# Revit family: DAL_A3-Gate-double
name_source: partatom
category: Doors
revit_build: Autodesk Revit 2016 (Build: 20150220_1215(x64)
units: mm (PartAtom-declared; Revit-internal decimal feet)

## family parameters
Always vertical = Yes
Cut with Voids When Loaded = No
Host = Wall
Room Calculation Point = No
Shared = No

## types (3) — shared parameters
Frame Projection Ext. = 25 mm  [stored 0.082021 ft]
Frame Projection Int. = 25 mm  [stored 0.082021 ft]
Frame Width = 75 mm  [stored 0.246063 ft]
Function = Interior
Wall Closure = By host

## per-type parameters (varying)
| type | Description | Height | Width |
| Gate-double - 3000mm |  | 2000 mm  [stored 6.56168 ft] | 1618 mm  [stored 5.3084 ft] |
| Gate-double | SPECIAL PURPOSE MILD STEEL ENTRANCE GATE MADE TO FIT OPENING ON SITE. TYPE + DESIGN TO H.O.A. APP. MEASURE ON SITE BEFORE MANUFACTURE. | 2550 mm  [stored 8.36614 ft] | 1872 mm |
| 1790X2000 |  | 2000 mm  [stored 6.56168 ft] | 1618 mm  [stored 5.3084 ft] |

note: [stored X ft] marks values corroborated as IEEE doubles in the binary element streams (Revit-internal decimal feet)

## geometry (parser evidence)
native form markers: Sweep x2
no freeform markers — native parametric forms only
